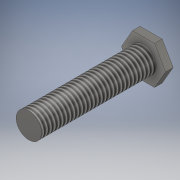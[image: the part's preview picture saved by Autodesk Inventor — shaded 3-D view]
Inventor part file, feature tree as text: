
AUTODESK INVENTOR PART (.ipt)
format: ipt  version: 2018 (Build 220112000, 112)  size: 114,176 bytes
history: native  units: in
note: dims shown in document units (in); Inventor stores cm internally (conversion verified against a paired STEP export)
features: extrude x2, sketch x2, thread x1
ambient origin geometry x8: Origin, YZ Plane, XZ Plane, XY Plane, X Axis, Y Axis, Z Axis, Center Point
bodies: Solid1 (feature_tree)
feature tree (5):
  extrude  "Extrusion1"  Depth=0.15in TaperAngle=0.0deg
  extrude  "Extrusion2"  Depth=2.25in TaperAngle=0.0deg
  thread  "Thread1"  [1 undecoded]
  sketch  "Sketch1"  dims[d0=0.75in d1=0.15in d2=0.0in]
  sketch  "Sketch2"  dims[d3=0.5in d4=2.25in d5=0.0in d6=1.0in d7=0.0in]
note: 1 required parameter value undecoded (feature->parameter linkage not recoverable at this tier; creation-order binding heuristic only, values carry confidence <= 0.55)
